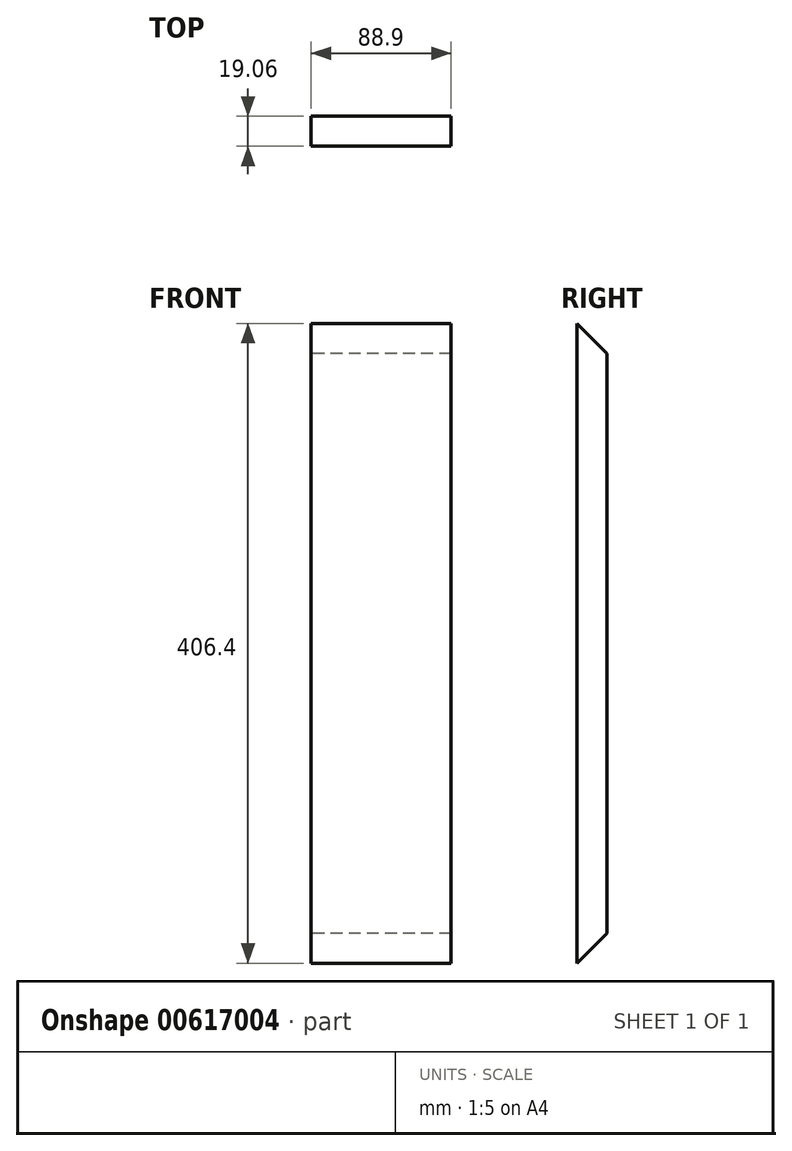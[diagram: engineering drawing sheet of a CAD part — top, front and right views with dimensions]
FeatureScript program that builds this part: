
annotation { "Feature Type Name" : "Feature", "Feature Type Description" : "" }
export const myFeature = defineFeature(function(context is Context, id is Id, definition is map)
    precondition{}
    {
        {
            var Q0;
            Q0=qCreatedBy(makeId("Right.planeOp"),FACE);
            var sketch = newSketch(context, id + "F0", { "sketchPlane" : qUnion([Q0])});
            skLineSegment(sketch, "E0.left", {"start": v(9.52, 184.15) * mm, "end": v(9.52, -184.15) * mm});
            skPoint(sketch, "E0.middle", {"position": v(0, 0) * mm});
            skLineSegment(sketch, "E1", {"start": v(-9.53, 203.2) * mm, "end": v(9.52, 184.15) * mm});
            skPoint(sketch, "E2.orphan", {"position": v(9.52, 203.2) * mm});
            skLineSegment(sketch, "E3", {"start": v(-9.52, -203.2) * mm, "end": v(9.52, -184.15) * mm});
            skPoint(sketch, "E0.top.start.orphan", {"position": v(9.53, -203.2) * mm});
            skLineSegment(sketch, "E4", {"start": v(-9.53, 203.2) * mm, "end": v(-9.53, 0) * mm});
            skLineSegment(sketch, "E5", {"start": v(-9.53, 0) * mm, "end": v(-9.53, -203.2) * mm});
            skSolve(sketch);
        }
        {
            var Q0;
            Q0=makeQuery(id+"F0.imprint","IMPRINT",FACE,{"disambiguationData":[TD([[makeQuery(id+"F0.imprint","IMPRINT",EDGE,{"derivedFrom":sQuery(id+"F0.wireOp",EDGE,"E0.left")}),-1.0]])]});
            extrude(context, id + "F1", {"entities" : qUnion([Q0]), "depth" : 88.9 * mm, "offsetDistance" : 25.4 * mm});
        }
    });
